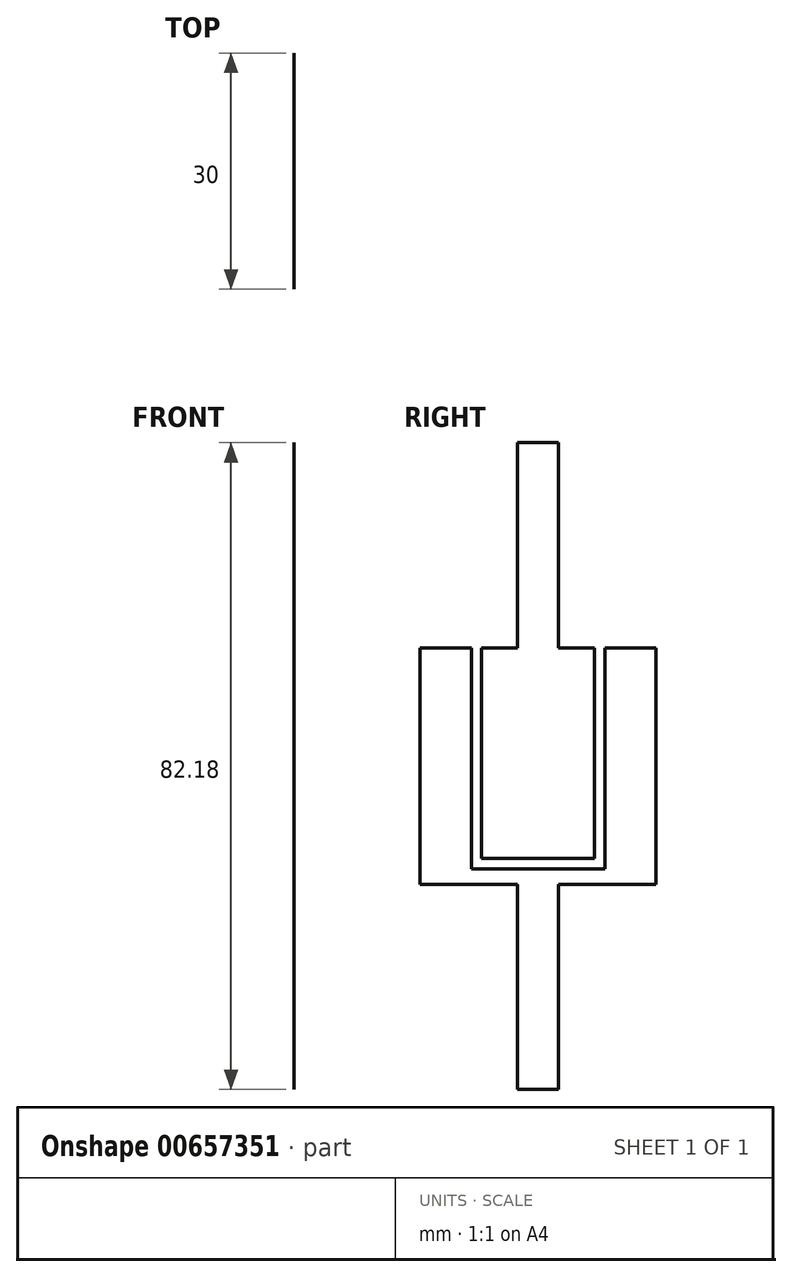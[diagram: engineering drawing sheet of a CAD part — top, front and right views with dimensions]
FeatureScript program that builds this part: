
annotation { "Feature Type Name" : "Feature", "Feature Type Description" : "" }
export const myFeature = defineFeature(function(context is Context, id is Id, definition is map)
    precondition{}
    {
        {
            var Q0;
            Q0=qCreatedBy(makeId("Right.planeOp"),FACE);
            var sketch = newSketch(context, id + "F0", { "sketchPlane" : qUnion([Q0])});
            skLineSegment(sketch, "E0", {"start": v(0, 0) * mm, "end": v(6.52, 0) * mm});
            skLineSegment(sketch, "E1", {"start": v(0, 0) * mm, "end": v(0, -30) * mm});
            skLineSegment(sketch, "E2", {"start": v(0, -30) * mm, "end": v(12.4, -30) * mm});
            skLineSegment(sketch, "E3", {"start": v(30, -30) * mm, "end": v(30, 0) * mm});
            skLineSegment(sketch, "E4", {"start": v(30, 0) * mm, "end": v(23.48, 0) * mm});
            skLineSegment(sketch, "E5.0", {"start": v(12.4, -30) * mm, "end": v(12.4, -51.07) * mm});
            skLineSegment(sketch, "E6", {"start": v(11.45, 0) * mm, "end": v(12.4, 0) * mm});
            skLineSegment(sketch, "E7.0", {"start": v(17.61, 0) * mm, "end": v(17.61, 26.09) * mm});
            skLineSegment(sketch, "E8.0", {"start": v(12.4, 0) * mm, "end": v(12.4, 26.09) * mm});
            skLineSegment(sketch, "E9", {"start": v(12.4, 26.09) * mm, "end": v(17.61, 26.09) * mm});
            skLineSegment(sketch, "E10.trimOffspring", {"start": v(17.61, 0) * mm, "end": v(22.17, 0) * mm});
            skLineSegment(sketch, "E11", {"start": v(30, -30) * mm, "end": v(17.6, -30) * mm});
            skLineSegment(sketch, "E12.trimOffspring", {"start": v(12.4, -30) * mm, "end": v(0, -30) * mm});
            skLineSegment(sketch, "E13", {"start": v(12, -30) * mm, "end": v(12.4, -30) * mm});
            skLineSegment(sketch, "E14", {"start": v(0, -30) * mm, "end": v(12, -30) * mm});
            skLineSegment(sketch, "E15", {"start": v(17.61, -56.09) * mm, "end": v(17.6, -30) * mm});
            skLineSegment(sketch, "E16.0", {"start": v(23.48, -28.04) * mm, "end": v(23.48, 0) * mm});
            skLineSegment(sketch, "E17.0", {"start": v(6.52, 0) * mm, "end": v(6.52, -28.04) * mm});
            skLineSegment(sketch, "E18.trimOffspring", {"start": v(17.6, -30) * mm, "end": v(30, -30) * mm});
            skPoint(sketch, "E19.trimOffspring.start.orphan", {"position": v(15, -30) * mm});
            skLineSegment(sketch, "E20.0", {"start": v(7.83, 0) * mm, "end": v(7.83, -26.74) * mm});
            skLineSegment(sketch, "E21.0", {"start": v(22.17, -26.74) * mm, "end": v(22.17, 0) * mm});
            skLineSegment(sketch, "E22.0", {"start": v(23.48, -28.04) * mm, "end": v(7.83, -28.04) * mm});
            skLineSegment(sketch, "E23", {"start": v(7.83, -28.04) * mm, "end": v(6.52, -28.04) * mm});
            skLineSegment(sketch, "E24", {"start": v(6.52, -28.04) * mm, "end": v(23.48, -28.04) * mm});
            skLineSegment(sketch, "E25.0", {"start": v(22.17, -26.74) * mm, "end": v(7.83, -26.74) * mm});
            skLineSegment(sketch, "E26", {"start": v(12.4, -51.07) * mm, "end": v(12.4, -56.09) * mm});
            skLineSegment(sketch, "E27", {"start": v(12.4, -56.09) * mm, "end": v(17.61, -56.09) * mm});
            skLineSegment(sketch, "E28", {"start": v(7.83, 0) * mm, "end": v(12.4, 0) * mm});
            skLineSegment(sketch, "E29.trimOffspring", {"start": v(23.48, 0) * mm, "end": v(30, 0) * mm});
            skLineSegment(sketch, "E30.trimOffspring", {"start": v(22.17, 0) * mm, "end": v(17.61, 0) * mm});
            skLineSegment(sketch, "E31.trimOffspring", {"start": v(12.4, 0) * mm, "end": v(9, 0) * mm});
            skSolve(sketch);
        }
        {
            var Q0;
            Q0=makeQuery(id+"F0.imprint","IMPRINT",FACE,{"disambiguationData":[TD([[makeQuery(id+"F0.imprint","IMPRINT",EDGE,{"derivedFrom":sQuery(id+"F0.wireOp",EDGE,"b56e8115-747c-47a9-926b-84bb7afac1cf.0")}),1.0]])]});
            var Q1;
            Q1=makeQuery(id+"F0.imprint","IMPRINT",FACE,{"disambiguationData":[TD([[makeQuery(id+"F0.imprint","IMPRINT",EDGE,{"derivedFrom":sQuery(id+"F0.wireOp",EDGE,"E0")}),-1.0]])]});
            var Q2;
            Q2=makeQuery(id+"F0.imprint","IMPRINT",FACE,{"disambiguationData":[TD([[makeQuery(id+"F0.imprint","IMPRINT",EDGE,{"derivedFrom":sQuery(id+"F0.wireOp",EDGE,"8dee40f3-ee80-49ba-9f93-c100ff8cb728.0")}),1.0]])]});
            var Q3;
            Q3=makeQuery(id+"F0.imprint","IMPRINT",FACE,{"disambiguationData":[TD([[makeQuery(id+"F0.imprint","IMPRINT",EDGE,{"derivedFrom":sQuery(id+"F0.wireOp",EDGE,"E7.0")}),1.0]])]});
            extrude(context, id + "F1", {"entities" : qUnion([Q0, Q1, Q2, Q3]), "depth" : 0 * mm, "offsetDistance" : 25 * mm});
        }
    });
